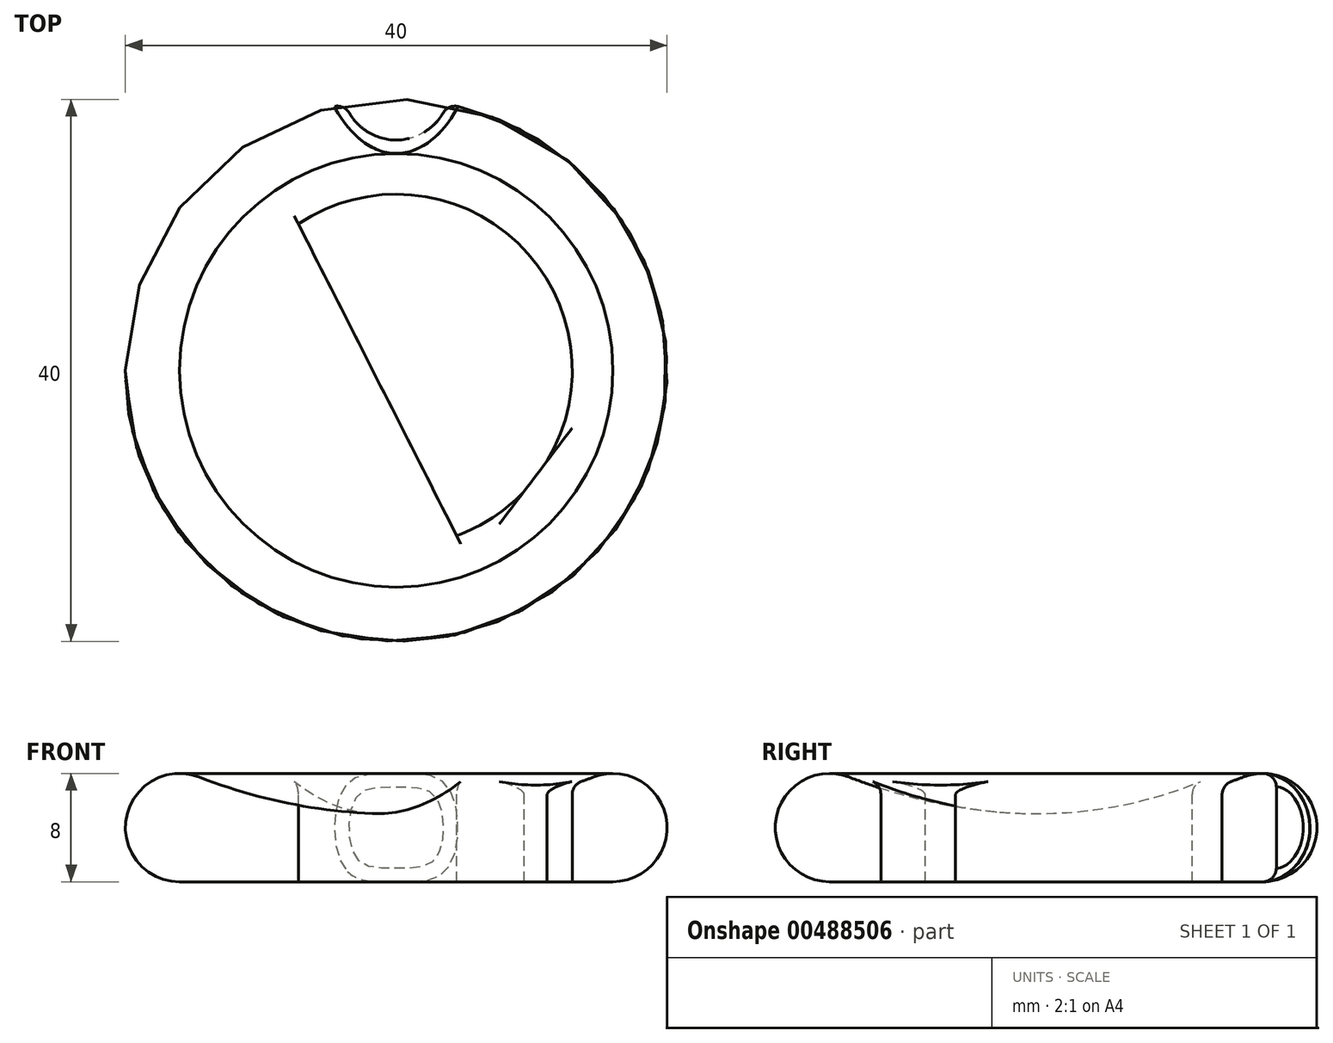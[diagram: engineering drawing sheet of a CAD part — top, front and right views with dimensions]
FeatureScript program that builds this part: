
annotation { "Feature Type Name" : "Feature", "Feature Type Description" : "" }
export const myFeature = defineFeature(function(context is Context, id is Id, definition is map)
    precondition{}
    {
        {
            var Q0;
            Q0=qCreatedBy(makeId("Front.planeOp"),FACE);
            var sketch = newSketch(context, id + "F0", { "sketchPlane" : qUnion([Q0])});
            skArc(sketch, "E0", {"start": v(-14.55, 7.73) * mm, "mid": v(-19.93, 4.74) * mm, "end": v(-16, 0) * mm});
            skArc(sketch, "E1", {"start": v(-14.55, 7.73) * mm, "mid": v(-7.4, 5.69) * mm, "end": v(0, 5) * mm});
            skLineSegment(sketch, "E2", {"start": v(0, 0) * mm, "end": v(-16, 0) * mm});
            skLineSegment(sketch, "E3", {"start": v(0, 0) * mm, "end": v(0, 5) * mm});
            skSolve(sketch);
        }
        {
            var Q0;
            Q0=makeQuery(id+"F0.imprint","IMPRINT",FACE,{"disambiguationData":[TD([[makeQuery(id+"F0.imprint","IMPRINT",EDGE,{"derivedFrom":sQuery(id+"F0.wireOp",EDGE,"E0")}),1.0]])]});
            var Q1;
            Q1=sQuery(id+"F0.wireOp",EDGE,"E3");
            revolve(context, id + "F1", {"entities" : qUnion([Q0]), "axis" : qUnion([Q1]), "revolveType" : RevolveType.FULL});
        }
        {
            var Q0;
            Q0=qCreatedBy(makeId("Top.planeOp"),FACE);
            cPlane(context, id + "F2", {"entities" : qUnion([Q0]), "cplaneType" : CPlaneType.OFFSET, "offset" : 10 * mm, "width" : 150 * mm, "height" : 150 * mm});
        }
        {
            var Q0;
            Q0=qCreatedBy(id+"F2.planeOp",FACE);
            var sketch = newSketch(context, id + "F3", { "sketchPlane" : qUnion([Q0])});
            skCircle(sketch, "E4", {"center": v(0, 0) * mm, "radius": 13 * mm});
            skLineSegment(sketch, "E5", {"start": v(5.47, -14.18) * mm, "end": v(17.48, 1.66) * mm});
            skLineSegment(sketch, "E6", {"start": v(17.48, 1.66) * mm, "end": v(15.43, 5.2) * mm});
            skLineSegment(sketch, "E7", {"start": v(5.47, -14.18) * mm, "end": v(-7.23, 10.8) * mm});
            skLineSegment(sketch, "E8", {"start": v(-4, 12.37) * mm, "end": v(6.22, -6.96) * mm});
            skLineSegment(sketch, "E9", {"start": v(6.22, -6.96) * mm, "end": v(12.87, 1.82) * mm});
            skLineSegment(sketch, "E10", {"start": v(12.87, 1.82) * mm, "end": v(15.43, 5.2) * mm});
            skSolve(sketch);
        }
        {
            var Q0;
            {var subQ0=sQuery(id+"F3.wireOp",EDGE,"E7");var subQ1=sQuery(id+"F3.wireOp",EDGE,"E4");var subQ2=makeQuery(id+"F3.imprint","INTERSECT",VERTEX,{"disambiguationData":[OD(0.0)],"derivedFrom":[subQ1,subQ0]});Q0=makeQuery(id+"F3.imprint","IMPRINT",FACE,{"disambiguationData":[TD([[makeQuery(id+"F3.imprint","IMPRINT",EDGE,{"disambiguationData":[TD([[subQ2,-1.0]])],"derivedFrom":subQ1}),1.0]])]});}
            extrude(context, id + "F4", {"entities" : qUnion([Q0]), "operationType" : NewBodyOperationType.REMOVE, "oppositeDirection" : true, "depth" : 25 * mm});
        }
        {
            var Q0;
            {var subQ0=sQuery(id+"F3.wireOp",EDGE,"E8");Q0=makeQuery(id+"F3.imprint","IMPRINT",FACE,{"disambiguationData":[TD([[makeQuery(id+"F3.imprint","IMPRINT",EDGE,{"derivedFrom":subQ0}),1.0]])]});}
            extrude(context, id + "F5", {"entities" : qUnion([Q0]), "operationType" : NewBodyOperationType.REMOVE, "oppositeDirection" : true, "depth" : 25 * mm});
        }
        {
            var Q0;
            Q0=qCreatedBy(makeId("Front.planeOp"),FACE);
            var sketch = newSketch(context, id + "F6", { "sketchPlane" : qUnion([Q0])});
            skCircle(sketch, "E11", {"center": v(-13, 3) * mm, "radius": 3 * mm});
            skSolve(sketch);
        }
        {
            var Q0;
            Q0=sQuery(id+"F6.wireOp",EDGE,"E11");
            var Q1;
            Q1=sQuery(id+"F0.wireOp",EDGE,"E3");
            revolve(context, id + "F7", {"bodyType" : ToolBodyType.SURFACE, "surfaceEntities" : qUnion([Q0]), "axis" : qUnion([Q1]), "revolveType" : RevolveType.FULL});
        }
        {
            var Q0;
            Q0=qCreatedBy(makeId("Top.planeOp"),FACE);
            var sketch = newSketch(context, id + "F8", { "sketchPlane" : qUnion([Q0])});
            skCircle(sketch, "E12", {"center": v(0, 21) * mm, "radius": 4 * mm});
            skSolve(sketch);
        }
        {
            var Q0;
            Q0=makeQuery(id+"F8.imprint","IMPRINT",FACE,{"disambiguationData":[TD([[makeQuery(id+"F8.imprint","IMPRINT",EDGE,{"derivedFrom":sQuery(id+"F8.wireOp",EDGE,"E12")}),1.0]])]});
            var Q1;
            Q1=sQuery(id+"F8.wireOp",EDGE,"E12");
            extrude(context, id + "F9", {"entities" : qUnion([Q0]), "operationType" : NewBodyOperationType.REMOVE, "surfaceEntities" : qUnion([Q1]), "depth" : 25.5 * mm});
        }
        {
            var Q0;
            Q0=makeQuery(id+"F9.boolean.opBoolean","INTERSECT",EDGE,{"derivedFrom":[makeQuery(id+"F1.opRevolve","SWEPT_FACE",FACE,{"disambiguationData":[OSD([sQuery(id+"F0.wireOp",EDGE,"E0")])]}),makeQuery(id+"F9.opExtrude","SWEPT_FACE",FACE,{"disambiguationData":[OSD([sQuery(id+"F8.wireOp",EDGE,"E12")])]})]});
            fillet(context, id + "F10", {"entities" : qUnion([Q0]), "radius" : 1 * mm, "tangentPropagation" : true, "allowEdgeOverflow" : false});
        }
        {
            var Q0;
            Q0=makeQuery(id+"F4.boolean.opBoolean","INTERSECT",EDGE,{"derivedFrom":[makeQuery(id+"F1.opRevolve","SWEPT_FACE",FACE,{"disambiguationData":[OSD([sQuery(id+"F0.wireOp",EDGE,"E1")])]}),makeQuery(id+"F4.opExtrude","SWEPT_FACE",FACE,{"disambiguationData":[OSD([sQuery(id+"F3.wireOp",EDGE,"E4")])]})]});
            fillet(context, id + "F11", {"entities" : qUnion([Q0]), "radius" : 1 * mm, "tangentPropagation" : true, "allowEdgeOverflow" : false});
        }
        {
            var Q0;
            Q0=makeQuery(id+"F5.boolean.opBoolean","INTERSECT",EDGE,{"derivedFrom":[makeQuery(id+"F1.opRevolve","SWEPT_FACE",FACE,{"disambiguationData":[OSD([sQuery(id+"F0.wireOp",EDGE,"E1")])]}),makeQuery(id+"F5.opExtrude","SWEPT_FACE",FACE,{"disambiguationData":[OSD([sQuery(id+"F3.wireOp",EDGE,"E4")])]})]});
            fillet(context, id + "F12", {"entities" : qUnion([Q0]), "radius" : 1 * mm, "tangentPropagation" : true, "allowEdgeOverflow" : false});
        }
    });
